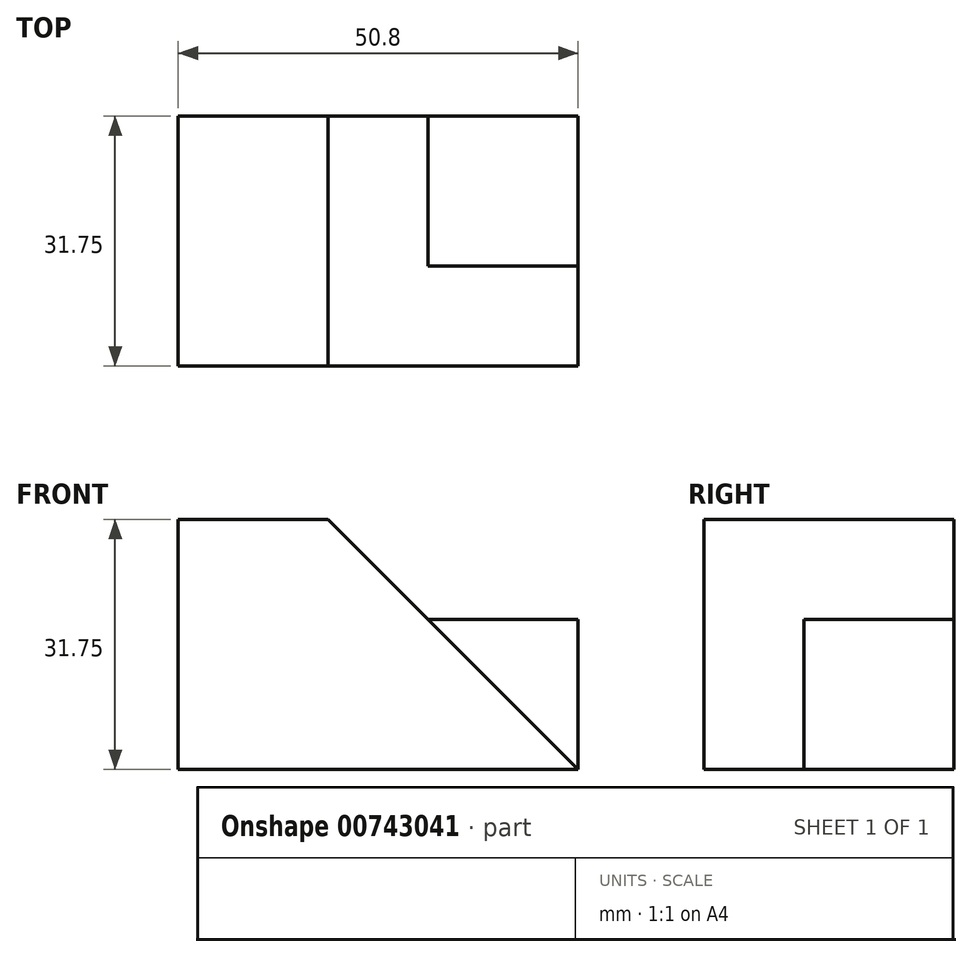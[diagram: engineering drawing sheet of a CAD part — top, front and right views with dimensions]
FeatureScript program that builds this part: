
annotation { "Feature Type Name" : "Feature", "Feature Type Description" : "" }
export const myFeature = defineFeature(function(context is Context, id is Id, definition is map)
    precondition{}
    {
        {
            var Q0;
            Q0=qCreatedBy(makeId("Front.planeOp"),FACE);
            var sketch = newSketch(context, id + "F0", { "sketchPlane" : qUnion([Q0])});
            skLineSegment(sketch, "E0", {"start": v(0, 0) * mm, "end": v(50.8, 0) * mm});
            skLineSegment(sketch, "E1", {"start": v(50.8, 0) * mm, "end": v(50.8, 31.75) * mm});
            skLineSegment(sketch, "E2", {"start": v(50.8, 31.75) * mm, "end": v(0, 31.75) * mm});
            skLineSegment(sketch, "E3", {"start": v(0, 31.75) * mm, "end": v(0, 0) * mm});
            skSolve(sketch);
        }
        {
            var Q0;
            Q0=makeQuery(id+"F0.imprint","IMPRINT",FACE,{"disambiguationData":[TD([[makeQuery(id+"F0.imprint","IMPRINT",EDGE,{"derivedFrom":sQuery(id+"F0.wireOp",EDGE,"E0")}),1.0]])]});
            extrude(context, id + "F1", {"entities" : qUnion([Q0]), "depth" : 31.75 * mm, "offsetDistance" : 25.4 * mm});
        }
        {
            var Q0;
            Q0=makeQuery(id+"F1.opExtrude","CAP_FACE",FACE,{"disambiguationData":[OSD([sQuery(id+"F0.wireOp",EDGE,"E0"),sQuery(id+"F0.wireOp",EDGE,"E1"),sQuery(id+"F0.wireOp",EDGE,"E2"),sQuery(id+"F0.wireOp",EDGE,"E3")])],"isStart":false});
            var sketch = newSketch(context, id + "F2", { "sketchPlane" : qUnion([Q0])});
            skLineSegment(sketch, "E4", {"start": v(50.8, 0) * mm, "end": v(19.05, 31.75) * mm});
            skSolve(sketch);
        }
        {
            var Q0;
            Q0 = qSketchRegion(id + "F2", true);
            var Q1;
            {var subQ0=sQuery(id+"F2.wireOp",EDGE,"E4");Q1=makeQuery(id+"F2.imprint","IMPRINT",FACE,{"disambiguationData":[TD([[makeQuery(id+"F2.imprint","IMPRINT",EDGE,{"derivedFrom":subQ0}),-1.0]])]});}
            extrude(context, id + "F3", {"entities" : qUnion([Q0, Q1]), "operationType" : NewBodyOperationType.REMOVE, "oppositeDirection" : true, "depth" : 12.7 * mm, "offsetDistance" : 25.4 * mm});
        }
        {
            var Q0;
            Q0=makeQuery(id+"F3.boolean.opBoolean","COPY",FACE,{"derivedFrom":makeQuery(id+"F3.opExtrude","CAP_FACE",FACE,{"disambiguationData":[OSD([sQuery(id+"F0.wireOp",EDGE,"E1"),sQuery(id+"F0.wireOp",EDGE,"E2"),sQuery(id+"F2.wireOp",EDGE,"E4")])],"isStart":false})});
            var sketch = newSketch(context, id + "F4", { "sketchPlane" : qUnion([Q0])});
            skLineSegment(sketch, "E5", {"start": v(50.8, 0) * mm, "end": v(50.8, 19.05) * mm});
            skLineSegment(sketch, "E6", {"start": v(50.8, 19.05) * mm, "end": v(50.8, 19.05) * mm});
            skLineSegment(sketch, "E7", {"start": v(50.8, 19.05) * mm, "end": v(31.75, 19.05) * mm});
            skSolve(sketch);
        }
        {
            var Q0;
            {var subQ0=sQuery(id+"F4.wireOp",EDGE,"E7");Q0=makeQuery(id+"F4.imprint","IMPRINT",FACE,{"disambiguationData":[TD([[makeQuery(id+"F4.imprint","IMPRINT",EDGE,{"derivedFrom":subQ0}),-1.0]])]});}
            extrude(context, id + "F5", {"entities" : qUnion([Q0]), "operationType" : NewBodyOperationType.REMOVE, "oppositeDirection" : true, "depth" : 25.4 * mm, "offsetDistance" : 25.4 * mm});
        }
    });
